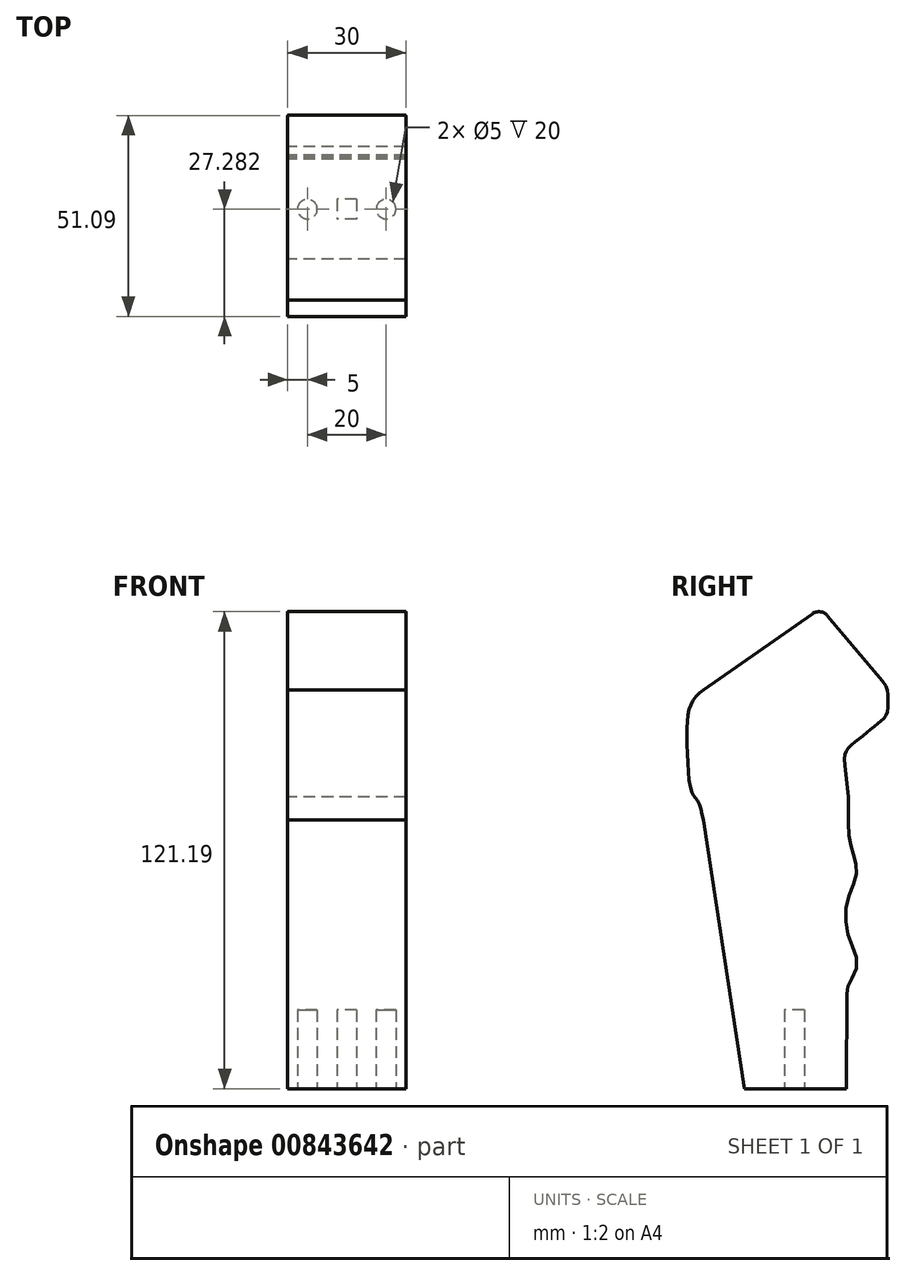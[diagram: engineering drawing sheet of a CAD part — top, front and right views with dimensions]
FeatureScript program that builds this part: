
annotation { "Feature Type Name" : "Feature", "Feature Type Description" : "" }
export const myFeature = defineFeature(function(context is Context, id is Id, definition is map)
    precondition{}
    {
        {
            var Q0;
            Q0=qCreatedBy(makeId("Right.planeOp"),FACE);
            var sketch = newSketch(context, id + "F0", { "sketchPlane" : qUnion([Q0])});
            skLineSegment(sketch, "E0", {"start": v(3.9, 126.96) * mm, "end": v(17.77, 110.43) * mm});
            skFitSpline(sketch, "E1", {"points": [v(8.75, 6.81) * mm, v(8.78, 28.68) * mm, v(9.2, 33.1) * mm, v(11.36, 38.41) * mm, v(9.27, 45.44) * mm, v(8.97, 54.56) * mm, v(11.28, 61.46) * mm, v(10.32, 66.79) * mm, v(9.28, 71.8) * mm, v(9.16, 80.97) * mm], "startDerivative": vector(-1.7, 55.25) * mm, "endDerivative": vector(-0.95, 55.3) * mm});
            skLineSegment(sketch, "E2", {"start": v(9.16, 80.97) * mm, "end": v(8.3, 88.97) * mm});
            skFitSpline(sketch, "E3", {"points": [v(8.3, 88.97) * mm, v(9.07, 93.18) * mm, v(12.76, 96.33) * mm, v(16.61, 99.55) * mm, v(18.85, 101.88) * mm, v(19.27, 105.84) * mm, v(17.77, 110.43) * mm], "startDerivative": vector(-4.42, 42.26) * mm, "endDerivative": vector(-26.89, 32.04) * mm});
            skLineSegment(sketch, "E4", {"start": v(0, 127.47) * mm, "end": v(-27.64, 108.13) * mm});
            skArc(sketch, "E5", {"start": v(3.9, 126.96) * mm, "mid": v(2.05, 127.97) * mm, "end": v(0, 127.47) * mm});
            skFitSpline(sketch, "E6", {"points": [v(-27.64, 108.13) * mm, v(-30.9, 104.27) * mm, v(-31.8, 95.59) * mm, v(-30.57, 82.05) * mm, v(-29.22, 80.19) * mm, v(-27.64, 75.08) * mm], "startDerivative": vector(-22.98, -17.65) * mm, "endDerivative": vector(8.17, -31.45) * mm});
            skLineSegment(sketch, "E7", {"start": v(-27.64, 75.08) * mm, "end": v(-17.25, 6.81) * mm});
            skLineSegment(sketch, "E8", {"start": v(-17.25, 6.81) * mm, "end": v(8.75, 6.81) * mm});
            skSolve(sketch);
        }
        {
            var Q0;
            Q0 = qSketchRegion(id + "F0", true);
            extrude(context, id + "F1", {"entities" : qUnion([Q0]), "endBound" : BoundingType.SYMMETRIC, "depth" : 30 * mm, "offsetDistance" : 25 * mm});
        }
        {
            var Q0;
            Q0=makeQuery(id+"F1.opExtrude","SWEPT_FACE",FACE,{"disambiguationData":[OSD([sQuery(id+"F0.wireOp",EDGE,"E8")])]});
            var sketch = newSketch(context, id + "F2", { "sketchPlane" : qUnion([Q0])});
            skCircle(sketch, "E9", {"center": v(-10, 4.54) * mm, "radius": 2.5 * mm});
            skCircle(sketch, "E10", {"center": v(10, 4.54) * mm, "radius": 2.5 * mm});
            skLineSegment(sketch, "E11.bottom", {"start": v(2.52, 2.04) * mm, "end": v(-2.52, 2.04) * mm});
            skLineSegment(sketch, "E11.top", {"start": v(2.52, 7.03) * mm, "end": v(-2.52, 7.03) * mm});
            skLineSegment(sketch, "E11.left", {"start": v(2.52, 2.04) * mm, "end": v(2.52, 7.03) * mm});
            skLineSegment(sketch, "E11.right", {"start": v(-2.52, 2.04) * mm, "end": v(-2.52, 7.03) * mm});
            skPoint(sketch, "E11.middle", {"position": v(0, 4.54) * mm});
            skSolve(sketch);
        }
        {
            var Q0;
            Q0=makeQuery(id+"F2.imprint","IMPRINT",FACE,{"disambiguationData":[TD([[makeQuery(id+"F2.imprint","IMPRINT",EDGE,{"derivedFrom":sQuery(id+"F2.wireOp",EDGE,"E11.bottom")}),-1.0]])]});
            var Q1;
            Q1=makeQuery(id+"F2.imprint","IMPRINT",FACE,{"disambiguationData":[TD([[makeQuery(id+"F2.imprint","IMPRINT",EDGE,{"derivedFrom":sQuery(id+"F2.wireOp",EDGE,"E9")}),1.0]])]});
            var Q2;
            Q2=makeQuery(id+"F2.imprint","IMPRINT",FACE,{"disambiguationData":[TD([[makeQuery(id+"F2.imprint","IMPRINT",EDGE,{"derivedFrom":sQuery(id+"F2.wireOp",EDGE,"E10")}),1.0]])]});
            extrude(context, id + "F3", {"entities" : qUnion([Q0, Q1, Q2]), "operationType" : NewBodyOperationType.REMOVE, "oppositeDirection" : true, "depth" : 20 * mm, "offsetDistance" : 25 * mm});
        }
    });
